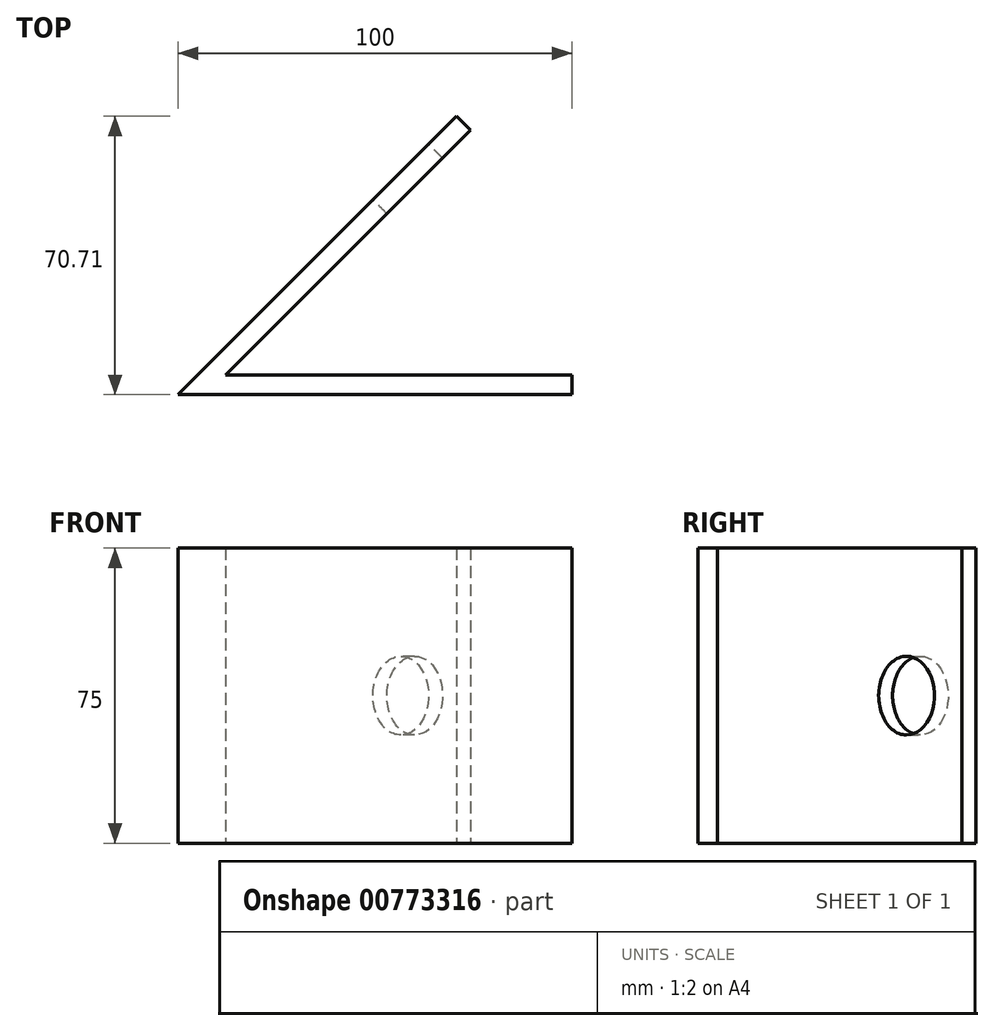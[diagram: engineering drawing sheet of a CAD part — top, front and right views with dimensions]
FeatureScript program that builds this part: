
annotation { "Feature Type Name" : "Feature", "Feature Type Description" : "" }
export const myFeature = defineFeature(function(context is Context, id is Id, definition is map)
    precondition{}
    {
        {
            var Q0;
            Q0=qCreatedBy(makeId("Top.planeOp"),FACE);
            var sketch = newSketch(context, id + "F0", { "sketchPlane" : qUnion([Q0])});
            skLineSegment(sketch, "E0", {"start": v(50, 0) * mm, "end": v(-50, 0) * mm});
            skLineSegment(sketch, "E1", {"start": v(-50, 0) * mm, "end": v(20.71, 70.71) * mm});
            skLineSegment(sketch, "E2", {"start": v(20.71, 70.71) * mm, "end": v(24.25, 67.18) * mm});
            skLineSegment(sketch, "E3", {"start": v(50, 0) * mm, "end": v(50, 5) * mm});
            skLineSegment(sketch, "E4", {"start": v(50, 5) * mm, "end": v(-37.93, 5) * mm});
            skLineSegment(sketch, "E5", {"start": v(-37.93, 5) * mm, "end": v(24.25, 67.18) * mm});
            skSolve(sketch);
        }
        {
            var Q0;
            Q0 = qSketchRegion(id + "F0", true);
            extrude(context, id + "F1", {"entities" : qUnion([Q0]), "depth" : 75 * mm, "offsetDistance" : 25 * mm});
        }
        {
            var Q0;
            Q0=makeQuery(id+"F1.opExtrude","SWEPT_FACE",FACE,{"disambiguationData":[OSD([sQuery(id+"F0.wireOp",EDGE,"E1")])]});
            var sketch = newSketch(context, id + "F2", { "sketchPlane" : qUnion([Q0])});
            skLineSegment(sketch, "E6", {"start": v(-44.64, 75) * mm, "end": v(-44.64, 0) * mm, "construction": true});
            skLineSegment(sketch, "E7", {"start": v(-64.64, 37.5) * mm, "end": v(35.36, 37.5) * mm, "construction": true});
            skPoint(sketch, "E8", {"position": v(-44.64, 37.5) * mm});
            skCircle(sketch, "E9", {"center": v(-44.64, 37.5) * mm, "radius": 10 * mm});
            skSolve(sketch);
        }
        {
            var Q0;
            Q0=makeQuery(id+"F2.imprint","IMPRINT",FACE,{"disambiguationData":[TD([[makeQuery(id+"F2.imprint","IMPRINT",EDGE,{"derivedFrom":sQuery(id+"F2.wireOp",EDGE,"E9")}),1.0]])]});
            var Q1;
            Q1=sQuery(id+"F2.wireOp",EDGE,"E9");
            extrude(context, id + "F3", {"entities" : qUnion([Q0]), "operationType" : NewBodyOperationType.REMOVE, "surfaceEntities" : qUnion([Q1]), "oppositeDirection" : true, "depth" : 25 * mm, "offsetDistance" : 25 * mm});
        }
    });
